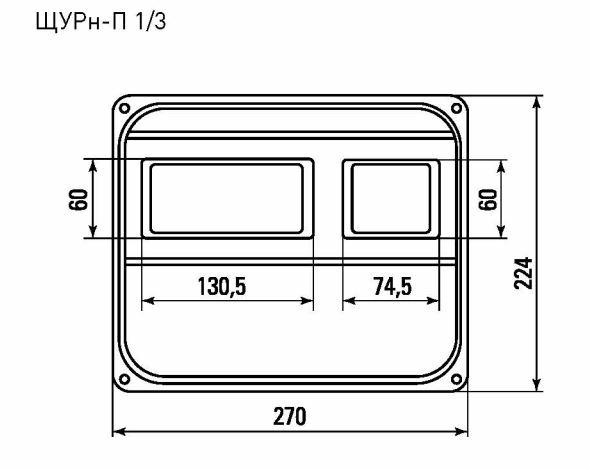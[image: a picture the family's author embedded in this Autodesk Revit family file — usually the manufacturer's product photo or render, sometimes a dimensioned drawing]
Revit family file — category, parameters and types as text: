
# Revit family: EKF_EE_КорпусЩО-70СварнойUnit_PROxima
name_source: partatom
category: Электрооборудование
units: mm (PartAtom-declared; Revit-internal decimal feet)

## family parameters
Всегда вертикально = Нет
На основе рабочей плоскости = Да
Общий = Да
При загрузке вырезать с полостями = Нет
Размер круглого соединителя = Использовать диаметр
Тип детали = Силовой щит
Точка расчета площади = Нет

## types (6) — shared parameters
ADSK_Единица измерения = шт.
ADSK_Завод-изготовитель = EKF
ADSK_Количество = 1
ADSK_Марка = Корпус ЩО-70 Unit
ADSK_Материал = RAL 7035_Сталь
ADSK_Обозначение = Корпус ЩО-70 Unit
ADSK_Размер_Глубина = 600 мм
D = 9 мм
t = 1 мм
ВертПроф_Отступ = 30 мм
Изготовитель = EKF
Отметка по умолчанию = 1219 мм
Отступ = 20 мм
РП450 = Вл_EKF_EE_РейкаПоперечнаяUNIT_PROxima : Рейка поперечная для ВРУ Unit глубиной 450мм EKF PROxima
РП600 = Вл_EKF_EE_РейкаПоперечнаяUNIT_PROxima : Рейка поперечная для ВРУ Unit глубиной 600мм EKF PROxima
РП_Отступ = 44 мм
РейкаПопереч_Шаг = 917 мм
РейкаПоперечная = Вл_EKF_EE_РейкаПоперечнаяUNIT_PROxima : Рейка поперечная для ВРУ Unit глубиной 600мм EKF PROxima
Серия номенклатуры = Unit PROxima
Степень защиты IP = -
Стойка_a = 24 мм
ТВ = EKF_2
Тип установки = -
zero-valued in all types: ADSK_Масса

## per-type parameters (varying)
| type | ADSK_Код изделия | ADSK_Размер_Высота | ADSK_Размер_Ширина | ЗСтенка_Ширина | Стойка_h | Тип |
| Корпус ЩО-70 Unit сварной (2000х1000х600) EKF PROxima | mb-05-07-04 | 2000 мм | 1000 мм | 760 мм | 1900 мм | 120 мм |
| Корпус ЩО-70 Unit сварной (2000х600х600) EKF PROxima | mb-05-07-06 | 2000 мм | 600 мм | 360 мм | 1900 мм | 121 мм |
| Корпус ЩО-70 Unit сварной (2000х800х600) EKF PROxima | mb-05-07-05 | 2000 мм | 800 мм | 560 мм | 1900 мм | 122 мм |
| Корпус ЩО-70 Unit сварной (2200х1000х600) EKF PROxima | mb-05-07-09 | 2200 мм | 1000 мм | 760 мм | 2100 мм | 123 мм |
| Корпус ЩО-70 Unit сварной (2200х600х600) EKF PROxima | mb-05-07-03 | 2200 мм | 600 мм | 360 мм | 2100 мм | 124 мм |
| Корпус ЩО-70 Unit сварной (2200х800х600) EKF PROxima | mb-05-07-01 | 2200 мм | 800 мм | 560 мм | 2100 мм | 125 мм |

note: column(s) folded — value = type name in every type: ADSK_Наименование
